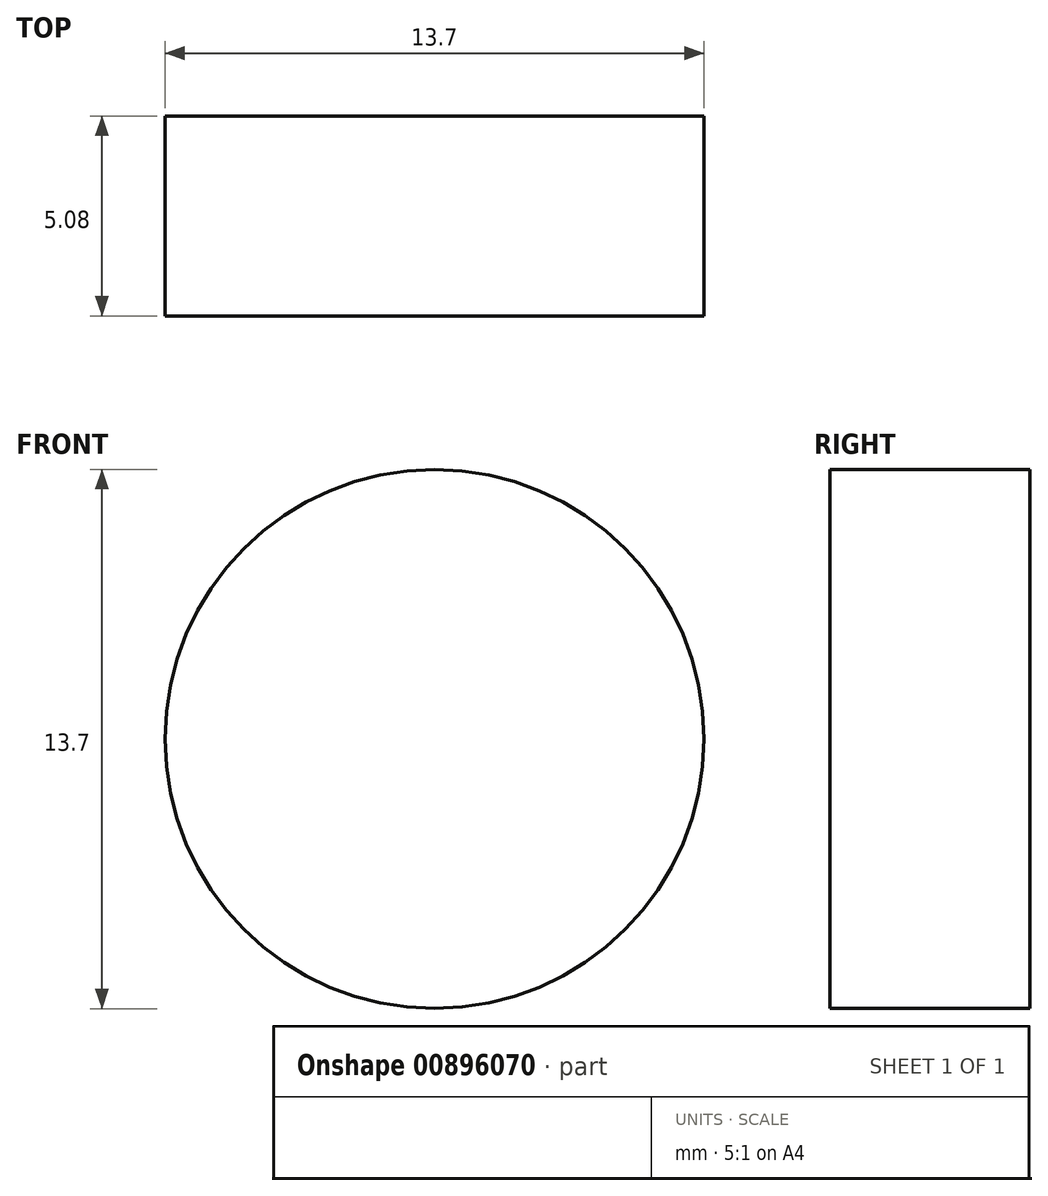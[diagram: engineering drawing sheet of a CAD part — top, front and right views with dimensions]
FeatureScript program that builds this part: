
annotation { "Feature Type Name" : "Feature", "Feature Type Description" : "" }
export const myFeature = defineFeature(function(context is Context, id is Id, definition is map)
    precondition{}
    {
        {
            var Q0;
            Q0=qCreatedBy(makeId("Front.planeOp"),FACE);
            var sketch = newSketch(context, id + "F0", { "sketchPlane" : qUnion([Q0])});
            skCircle(sketch, "E0", {"center": v(0, 0) * mm, "radius": 6.85 * mm});
            skSolve(sketch);
        }
        {
            var Q0;
            Q0=makeQuery(id+"F0.imprint","IMPRINT",FACE,{"disambiguationData":[TD([[makeQuery(id+"F0.imprint","IMPRINT",EDGE,{"derivedFrom":sQuery(id+"F0.wireOp",EDGE,"E0")}),1.0]])]});
            extrude(context, id + "F1", {"entities" : qUnion([Q0]), "depth" : 5.08 * mm, "offsetDistance" : 25.4 * mm});
        }
    });
